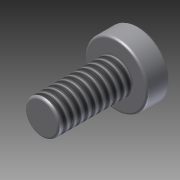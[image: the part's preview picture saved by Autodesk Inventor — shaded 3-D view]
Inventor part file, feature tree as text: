
AUTODESK INVENTOR PART (.ipt)
format: ipt  version: 2011 (Build 150239000, 239)  size: 124,928 bytes
history: native  units: in
note: dims shown in document units (in); Inventor stores cm internally (conversion verified against a paired STEP export)
features: extrude x3, sketch x3, thread x1, fillet x1
ambient origin geometry x8: Origin, YZ Plane, XZ Plane, XY Plane, X Axis, Y Axis, Z Axis, Center Point
bodies: Solid1 (feature_tree)
feature tree (8):
  extrude  "Extrusion1"  Depth=0.1in TaperAngle=0.0deg
  extrude  "Extrusion2"  Depth=0.325in TaperAngle=0.0deg
  extrude  "Extrusion3"  Depth=0.1in TaperAngle=0.0deg
  thread  "Thread1"  [1 undecoded]
  fillet  "Fillet1"  Radius=0.01in
  sketch  "Sketch1"  dims[d0=0.275in d1=0.1in d2=0.0in]
  sketch  "Sketch2"  dims[d3=0.15in d4=0.325in d5=0.0in]
  sketch  "Sketch3"  dims[d6=0.1in d7=0.1in d8=0.0in d9=1.0in d10=0.0in d11=0.01in]
note: 1 required parameter value undecoded (feature->parameter linkage not recoverable at this tier; creation-order binding heuristic only, values carry confidence <= 0.55)
